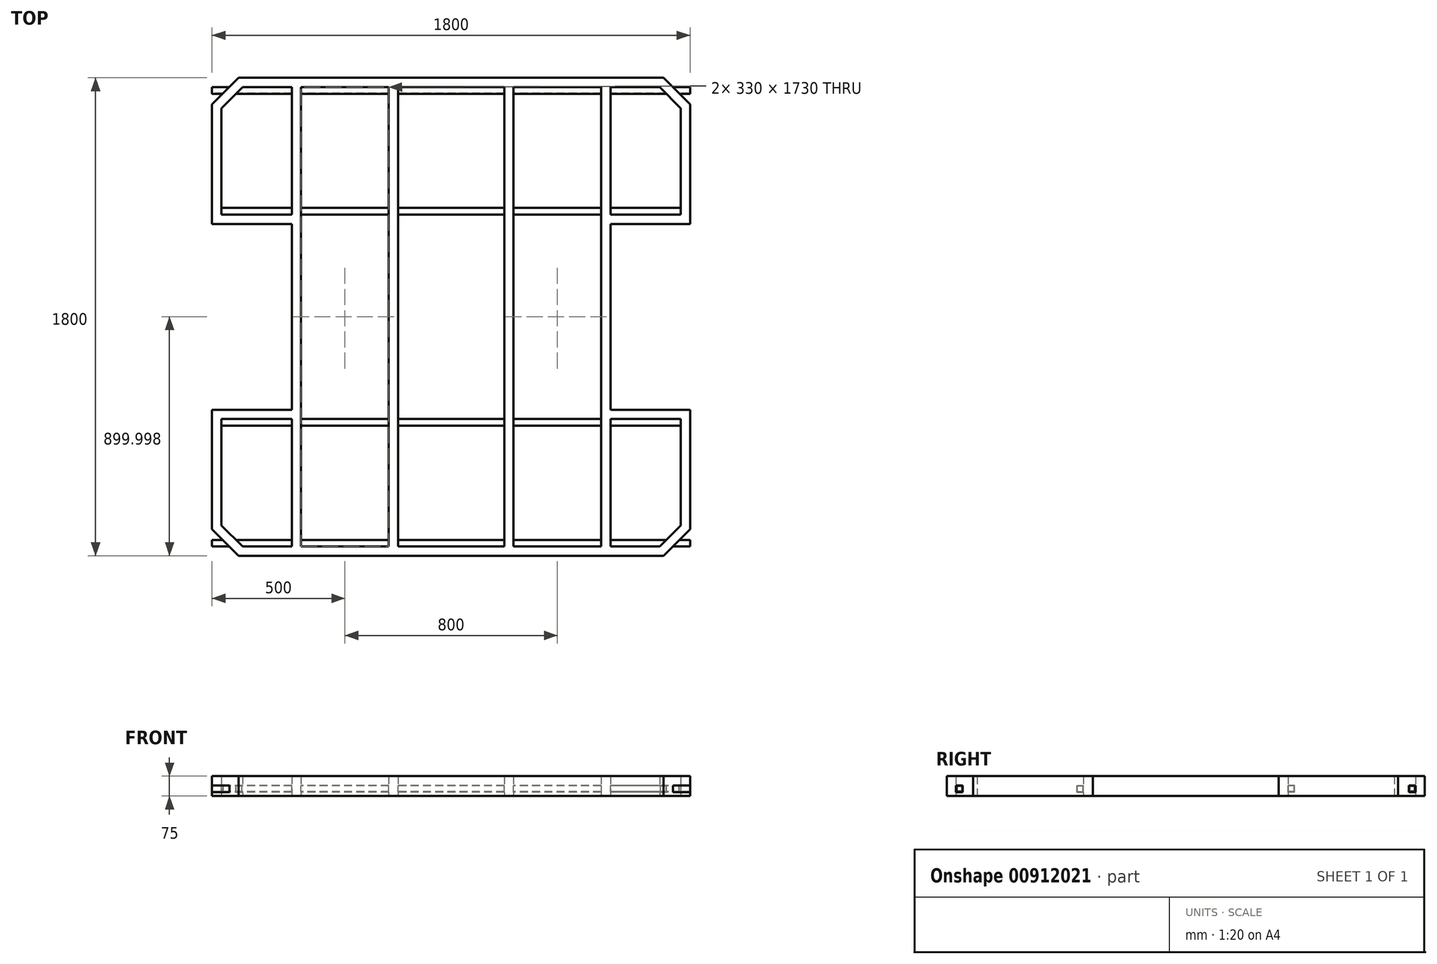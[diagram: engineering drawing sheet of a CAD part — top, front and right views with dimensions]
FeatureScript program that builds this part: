
annotation { "Feature Type Name" : "Feature", "Feature Type Description" : "" }
export const myFeature = defineFeature(function(context is Context, id is Id, definition is map)
    precondition{}
    {
        {
            var Q0;
            Q0=qCreatedBy(makeId("Top.planeOp"),FACE);
            var sketch = newSketch(context, id + "F0", { "sketchPlane" : qUnion([Q0])});
            skLineSegment(sketch, "E0.bottom", {"start": v(-100, 518.45) * mm, "end": v(-1700, 518.45) * mm});
            skLineSegment(sketch, "E0.top", {"start": v(-100, 2318.45) * mm, "end": v(-1700, 2318.45) * mm});
            skLineSegment(sketch, "E0.left", {"start": v(0, 618.45) * mm, "end": v(0, 1068.45) * mm});
            skLineSegment(sketch, "E1", {"start": v(-1800, 2218.45) * mm, "end": v(-1700, 2318.45) * mm});
            skLineSegment(sketch, "E2", {"start": v(-100, 2318.45) * mm, "end": v(0, 2218.45) * mm});
            skLineSegment(sketch, "E3", {"start": v(0, 618.45) * mm, "end": v(-100, 518.45) * mm});
            skPoint(sketch, "E4.orphan", {"position": v(-1344.08, 2218.45) * mm});
            skLineSegment(sketch, "E5", {"start": v(-1700, 518.45) * mm, "end": v(-1800, 618.45) * mm});
            skLineSegment(sketch, "E6", {"start": v(-1800, 618.45) * mm, "end": v(-1800, 1068.45) * mm});
            skLineSegment(sketch, "E7.bottom", {"start": v(-1900, 1768.45) * mm, "end": v(-1500, 1768.45) * mm});
            skLineSegment(sketch, "E7.top", {"start": v(-1900, 1068.45) * mm, "end": v(-1500, 1068.45) * mm});
            skLineSegment(sketch, "E7.left", {"start": v(-1900, 1768.45) * mm, "end": v(-1900, 1068.45) * mm});
            skLineSegment(sketch, "E7.right", {"start": v(-1500, 1768.45) * mm, "end": v(-1500, 1068.45) * mm});
            skLineSegment(sketch, "E8.bottom", {"start": v(-300, 1768.45) * mm, "end": v(100, 1768.45) * mm});
            skLineSegment(sketch, "E8.top", {"start": v(-300, 1068.45) * mm, "end": v(100, 1068.45) * mm});
            skLineSegment(sketch, "E8.left", {"start": v(-300, 1768.45) * mm, "end": v(-300, 1068.45) * mm});
            skLineSegment(sketch, "E8.right", {"start": v(100, 1768.45) * mm, "end": v(100, 1068.45) * mm});
            skLineSegment(sketch, "E9.trimOffspring", {"start": v(-1800, 1768.45) * mm, "end": v(-1800, 2218.45) * mm});
            skLineSegment(sketch, "E10.trimOffspring", {"start": v(0, 1768.45) * mm, "end": v(0, 2218.45) * mm});
            skSolve(sketch);
        }
        {
            var Q0;
            Q0=makeQuery(id+"F0.imprint","IMPRINT",FACE,{"disambiguationData":[TD([[makeQuery(id+"F0.imprint","IMPRINT",EDGE,{"derivedFrom":sQuery(id+"F0.wireOp",EDGE,"E0.bottom")}),-1.0]])]});
            var sketch = newSketch(context, id + "F1", { "sketchPlane" : qUnion([Q0])});
            skLineSegment(sketch, "E11.0.0", {"start": v(-300, 1768.45) * mm, "end": v(0, 1768.45) * mm});
            skLineSegment(sketch, "E11.0.1", {"start": v(0, 1768.45) * mm, "end": v(0, 2218.45) * mm});
            skLineSegment(sketch, "E11.0.2", {"start": v(0, 2218.45) * mm, "end": v(-100, 2318.45) * mm});
            skLineSegment(sketch, "E11.0.3", {"start": v(-100, 2318.45) * mm, "end": v(-1700, 2318.45) * mm});
            skLineSegment(sketch, "E11.0.4", {"start": v(-1700, 2318.45) * mm, "end": v(-1800, 2218.45) * mm});
            skLineSegment(sketch, "E11.0.5", {"start": v(-1800, 2218.45) * mm, "end": v(-1800, 1768.45) * mm});
            skLineSegment(sketch, "E11.0.6", {"start": v(-1800, 1768.45) * mm, "end": v(-1500, 1768.45) * mm});
            skLineSegment(sketch, "E11.0.7", {"start": v(-1500, 1768.45) * mm, "end": v(-1500, 1068.45) * mm});
            skLineSegment(sketch, "E11.0.8", {"start": v(-1500, 1068.45) * mm, "end": v(-1800, 1068.45) * mm});
            skLineSegment(sketch, "E11.0.9", {"start": v(-1800, 1068.45) * mm, "end": v(-1800, 618.45) * mm});
            skLineSegment(sketch, "E11.0.10", {"start": v(-1800, 618.45) * mm, "end": v(-1700, 518.45) * mm});
            skLineSegment(sketch, "E11.0.11", {"start": v(-1700, 518.45) * mm, "end": v(-100, 518.45) * mm});
            skLineSegment(sketch, "E11.0.12", {"start": v(-100, 518.45) * mm, "end": v(0, 618.45) * mm});
            skLineSegment(sketch, "E11.0.13", {"start": v(0, 618.45) * mm, "end": v(0, 1068.45) * mm});
            skLineSegment(sketch, "E11.0.14", {"start": v(0, 1068.45) * mm, "end": v(-300, 1068.45) * mm});
            skLineSegment(sketch, "E11.0.15", {"start": v(-300, 1068.45) * mm, "end": v(-300, 1768.45) * mm});
            skLineSegment(sketch, "E12.0", {"start": v(-335, 1033.45) * mm, "end": v(-335, 1803.45) * mm});
            skLineSegment(sketch, "E12.1", {"start": v(-35, 1033.45) * mm, "end": v(-300, 1033.45) * mm});
            skLineSegment(sketch, "E12.2", {"start": v(-35, 632.95) * mm, "end": v(-35, 1033.45) * mm});
            skLineSegment(sketch, "E12.3", {"start": v(-114.5, 553.45) * mm, "end": v(-35, 632.95) * mm});
            skLineSegment(sketch, "E12.4", {"start": v(-1685.5, 553.45) * mm, "end": v(-1500, 553.45) * mm});
            skLineSegment(sketch, "E12.5", {"start": v(-1685.5, 2283.45) * mm, "end": v(-1765, 2203.95) * mm});
            skLineSegment(sketch, "E12.6", {"start": v(-114.5, 2283.45) * mm, "end": v(-300, 2283.45) * mm});
            skLineSegment(sketch, "E12.7", {"start": v(-35, 2203.95) * mm, "end": v(-114.5, 2283.45) * mm});
            skLineSegment(sketch, "E12.8", {"start": v(-35, 1803.45) * mm, "end": v(-35, 2203.95) * mm});
            skLineSegment(sketch, "E12.9", {"start": v(-1765, 2203.95) * mm, "end": v(-1765, 1803.45) * mm});
            skLineSegment(sketch, "E12.10", {"start": v(-1765, 1803.45) * mm, "end": v(-1500, 1803.45) * mm});
            skLineSegment(sketch, "E12.11", {"start": v(-1465, 1803.45) * mm, "end": v(-1465, 1033.45) * mm});
            skLineSegment(sketch, "E12.12", {"start": v(-1500, 1033.45) * mm, "end": v(-1765, 1033.45) * mm});
            skLineSegment(sketch, "E12.13", {"start": v(-1765, 1033.45) * mm, "end": v(-1765, 632.95) * mm});
            skLineSegment(sketch, "E12.14", {"start": v(-300, 1803.45) * mm, "end": v(-35, 1803.45) * mm});
            skLineSegment(sketch, "E12.15", {"start": v(-1765, 632.95) * mm, "end": v(-1685.5, 553.45) * mm});
            skLineSegment(sketch, "E13", {"start": v(-1465, 1803.45) * mm, "end": v(-1465, 2283.45) * mm});
            skLineSegment(sketch, "E14", {"start": v(-1500, 1803.45) * mm, "end": v(-1500, 2283.45) * mm});
            skLineSegment(sketch, "E15", {"start": v(-1465, 1033.45) * mm, "end": v(-1465, 553.45) * mm});
            skLineSegment(sketch, "E16", {"start": v(-1500, 1033.45) * mm, "end": v(-1500, 553.45) * mm});
            skLineSegment(sketch, "E17", {"start": v(-335, 1033.45) * mm, "end": v(-335, 553.45) * mm});
            skLineSegment(sketch, "E18", {"start": v(-300, 1033.45) * mm, "end": v(-300, 553.45) * mm});
            skLineSegment(sketch, "E19", {"start": v(-335, 1803.45) * mm, "end": v(-335, 2283.45) * mm});
            skLineSegment(sketch, "E20", {"start": v(-300, 1803.45) * mm, "end": v(-300, 2283.45) * mm});
            skLineSegment(sketch, "E21.trimOffspring", {"start": v(-1500, 2283.45) * mm, "end": v(-1685.5, 2283.45) * mm});
            skLineSegment(sketch, "E22.trimOffspring", {"start": v(-1465, 553.45) * mm, "end": v(-1135, 553.45) * mm});
            skLineSegment(sketch, "E23.trimOffspring", {"start": v(-875, 553.45) * mm, "end": v(-700, 553.45) * mm});
            skLineSegment(sketch, "E24.trimOffspring", {"start": v(-735, 2283.45) * mm, "end": v(-1100, 2283.45) * mm});
            skLineSegment(sketch, "E25", {"start": v(-875, 2283.45) * mm, "end": v(-735, 2283.45) * mm});
            skLineSegment(sketch, "E26", {"start": v(-875, 553.45) * mm, "end": v(-735, 553.45) * mm});
            skLineSegment(sketch, "E27", {"start": v(-1135, 2283.45) * mm, "end": v(-1135, 553.45) * mm});
            skLineSegment(sketch, "E28", {"start": v(-1100, 2283.45) * mm, "end": v(-1100, 553.45) * mm});
            skLineSegment(sketch, "E29", {"start": v(-700, 2283.45) * mm, "end": v(-700, 553.45) * mm});
            skLineSegment(sketch, "E30", {"start": v(-665, 2283.45) * mm, "end": v(-665, 553.45) * mm});
            skLineSegment(sketch, "E31.trimOffspring", {"start": v(-1135, 2283.45) * mm, "end": v(-1465, 2283.45) * mm});
            skLineSegment(sketch, "E32.trimOffspring", {"start": v(-700, 2283.45) * mm, "end": v(-875, 2283.45) * mm});
            skLineSegment(sketch, "E33.trimOffspring", {"start": v(-335, 2283.45) * mm, "end": v(-665, 2283.45) * mm});
            skLineSegment(sketch, "E34.trimOffspring", {"start": v(-300, 553.45) * mm, "end": v(-114.5, 553.45) * mm});
            skLineSegment(sketch, "E35.trimOffspring", {"start": v(-665, 553.45) * mm, "end": v(-335, 553.45) * mm});
            skLineSegment(sketch, "E36.trimOffspring", {"start": v(-1100, 553.45) * mm, "end": v(-735, 553.45) * mm});
            skSolve(sketch);
        }
        {
            var Q0;
            Q0 = qSketchRegion(id + "F1", true);
            extrude(context, id + "F2", {"entities" : qUnion([Q0]), "depth" : 75 * mm, "offsetDistance" : 25 * mm});
        }
        {
            var Q0;
            Q0=makeQuery(id+"F2.opExtrude","SWEPT_FACE",FACE,{"disambiguationData":[OSD([sQuery(id+"F1.wireOp",EDGE,"E11.0.9")])]});
            var sketch = newSketch(context, id + "F3", { "sketchPlane" : qUnion([Q0])});
            skLineSegment(sketch, "E37.0.1", {"start": v(-553.45, 15) * mm, "end": v(-553.45, 75) * mm});
            skLineSegment(sketch, "E37.0.2", {"start": v(-553.45, 75) * mm, "end": v(-1033.45, 75) * mm});
            skLineSegment(sketch, "E37.0.3", {"start": v(-1033.45, 75) * mm, "end": v(-1033.45, 15) * mm});
            skLineSegment(sketch, "E38.bottom", {"start": v(-1033.45, 40) * mm, "end": v(-1008.45, 40) * mm});
            skLineSegment(sketch, "E38.top", {"start": v(-1033.45, 15) * mm, "end": v(-1008.45, 15) * mm});
            skLineSegment(sketch, "E38.left", {"start": v(-1033.45, 40) * mm, "end": v(-1033.45, 15) * mm});
            skLineSegment(sketch, "E38.right", {"start": v(-1008.45, 40) * mm, "end": v(-1008.45, 15) * mm});
            skLineSegment(sketch, "E39.bottom", {"start": v(-553.45, 40) * mm, "end": v(-578.45, 40) * mm});
            skLineSegment(sketch, "E39.top", {"start": v(-553.45, 15) * mm, "end": v(-578.45, 15) * mm});
            skLineSegment(sketch, "E39.left", {"start": v(-553.45, 40) * mm, "end": v(-553.45, 15) * mm});
            skLineSegment(sketch, "E39.right", {"start": v(-578.45, 40) * mm, "end": v(-578.45, 15) * mm});
            skPoint(sketch, "E40.orphan", {"position": v(-1033.45, 0) * mm});
            skPoint(sketch, "E41.orphan", {"position": v(-553.45, 0) * mm});
            skLineSegment(sketch, "E42.0", {"start": v(-1031.85, 38.4) * mm, "end": v(-1010.05, 38.4) * mm});
            skLineSegment(sketch, "E42.1", {"start": v(-1031.85, 38.4) * mm, "end": v(-1031.85, 16.6) * mm});
            skLineSegment(sketch, "E42.2", {"start": v(-1031.85, 16.6) * mm, "end": v(-1010.05, 16.6) * mm});
            skLineSegment(sketch, "E42.3", {"start": v(-1010.05, 38.4) * mm, "end": v(-1010.05, 16.6) * mm});
            skLineSegment(sketch, "E43.0", {"start": v(-555.05, 38.4) * mm, "end": v(-576.85, 38.4) * mm});
            skLineSegment(sketch, "E43.1", {"start": v(-555.05, 38.4) * mm, "end": v(-555.05, 16.6) * mm});
            skLineSegment(sketch, "E43.2", {"start": v(-555.05, 16.6) * mm, "end": v(-576.85, 16.6) * mm});
            skLineSegment(sketch, "E43.3", {"start": v(-576.85, 38.4) * mm, "end": v(-576.85, 16.6) * mm});
            skSolve(sketch);
        }
        {
            var Q0;
            Q0 = qSketchRegion(id + "F3", true);
            extrude(context, id + "F4", {"entities" : qUnion([Q0]), "operationType" : NewBodyOperationType.ADD, "oppositeDirection" : true, "depth" : 1800 * mm, "offsetDistance" : 25 * mm});
        }
        {
            var Q0;
            Q0=makeQuery(id+"F2.opExtrude","CAP_FACE",FACE,{"disambiguationData":[OSD([sQuery(id+"F1.wireOp",EDGE,"E11.0.0"),sQuery(id+"F1.wireOp",EDGE,"E11.0.1"),sQuery(id+"F1.wireOp",EDGE,"E11.0.2"),sQuery(id+"F1.wireOp",EDGE,"E11.0.3"),sQuery(id+"F1.wireOp",EDGE,"E11.0.4"),sQuery(id+"F1.wireOp",EDGE,"E11.0.5"),sQuery(id+"F1.wireOp",EDGE,"E11.0.6"),sQuery(id+"F1.wireOp",EDGE,"E11.0.7"),sQuery(id+"F1.wireOp",EDGE,"E11.0.8"),sQuery(id+"F1.wireOp",EDGE,"E11.0.9"),sQuery(id+"F1.wireOp",EDGE,"E11.0.10"),sQuery(id+"F1.wireOp",EDGE,"E11.0.11"),sQuery(id+"F1.wireOp",EDGE,"E11.0.12"),sQuery(id+"F1.wireOp",EDGE,"E11.0.13"),sQuery(id+"F1.wireOp",EDGE,"E11.0.14"),sQuery(id+"F1.wireOp",EDGE,"E11.0.15"),sQuery(id+"F1.wireOp",EDGE,"E12.0"),sQuery(id+"F1.wireOp",EDGE,"E12.1"),sQuery(id+"F1.wireOp",EDGE,"E12.2"),sQuery(id+"F1.wireOp",EDGE,"E12.3"),sQuery(id+"F1.wireOp",EDGE,"E12.4"),sQuery(id+"F1.wireOp",EDGE,"E12.5"),sQuery(id+"F1.wireOp",EDGE,"E12.6"),sQuery(id+"F1.wireOp",EDGE,"E12.7"),sQuery(id+"F1.wireOp",EDGE,"E12.8"),sQuery(id+"F1.wireOp",EDGE,"E12.9"),sQuery(id+"F1.wireOp",EDGE,"E12.10"),sQuery(id+"F1.wireOp",EDGE,"E12.11"),sQuery(id+"F1.wireOp",EDGE,"E12.12"),sQuery(id+"F1.wireOp",EDGE,"E12.13"),sQuery(id+"F1.wireOp",EDGE,"E12.14"),sQuery(id+"F1.wireOp",EDGE,"E12.15"),sQuery(id+"F1.wireOp",EDGE,"E13"),sQuery(id+"F1.wireOp",EDGE,"E14"),sQuery(id+"F1.wireOp",EDGE,"E15"),sQuery(id+"F1.wireOp",EDGE,"E16"),sQuery(id+"F1.wireOp",EDGE,"E17"),sQuery(id+"F1.wireOp",EDGE,"E18"),sQuery(id+"F1.wireOp",EDGE,"E19"),sQuery(id+"F1.wireOp",EDGE,"E20"),sQuery(id+"F1.wireOp",EDGE,"E21.trimOffspring"),sQuery(id+"F1.wireOp",EDGE,"E22.trimOffspring"),sQuery(id+"F1.wireOp",EDGE,"E23.trimOffspring"),sQuery(id+"F1.wireOp",EDGE,"E24.trimOffspring"),sQuery(id+"F1.wireOp",EDGE,"E27"),sQuery(id+"F1.wireOp",EDGE,"E28"),sQuery(id+"F1.wireOp",EDGE,"E29"),sQuery(id+"F1.wireOp",EDGE,"E30"),sQuery(id+"F1.wireOp",EDGE,"E31.trimOffspring"),sQuery(id+"F1.wireOp",EDGE,"E32.trimOffspring"),sQuery(id+"F1.wireOp",EDGE,"E33.trimOffspring"),sQuery(id+"F1.wireOp",EDGE,"E34.trimOffspring"),sQuery(id+"F1.wireOp",EDGE,"E35.trimOffspring"),sQuery(id+"F1.wireOp",EDGE,"E36.trimOffspring")])],"isStart":false});
            var sketch = newSketch(context, id + "F5", { "sketchPlane" : qUnion([Q0])});
            skLineSegment(sketch, "E44", {"start": v(-1500, 1418.45) * mm, "end": v(-300, 1418.45) * mm});
            skSolve(sketch);
        }
        {
            var Q0;
            Q0=makeQuery(id+"F2.opExtrude","SWEPT_FACE",FACE,{"disambiguationData":[OSD([sQuery(id+"F1.wireOp",EDGE,"E11.0.3")])]});
            cPlane(context, id + "F6", {"entities" : qUnion([Q0]), "cplaneType" : CPlaneType.OFFSET, "offset" : 900 * mm, "oppositeDirection" : true, "width" : 150 * mm, "height" : 150 * mm});
        }
        {
            var Q0;
            Q0=makeQuery(id+"F2.opExtrude","SWEPT_BODY",BODY,{"disambiguationData":[OSD([sQuery(id+"F1.wireOp",EDGE,"E11.0.0"),sQuery(id+"F1.wireOp",EDGE,"E11.0.1"),sQuery(id+"F1.wireOp",EDGE,"E11.0.2"),sQuery(id+"F1.wireOp",EDGE,"E11.0.3"),sQuery(id+"F1.wireOp",EDGE,"E11.0.4"),sQuery(id+"F1.wireOp",EDGE,"E11.0.5"),sQuery(id+"F1.wireOp",EDGE,"E11.0.6"),sQuery(id+"F1.wireOp",EDGE,"E11.0.7"),sQuery(id+"F1.wireOp",EDGE,"E11.0.8"),sQuery(id+"F1.wireOp",EDGE,"E11.0.9"),sQuery(id+"F1.wireOp",EDGE,"E11.0.10"),sQuery(id+"F1.wireOp",EDGE,"E11.0.11"),sQuery(id+"F1.wireOp",EDGE,"E11.0.12"),sQuery(id+"F1.wireOp",EDGE,"E11.0.13"),sQuery(id+"F1.wireOp",EDGE,"E11.0.14"),sQuery(id+"F1.wireOp",EDGE,"E11.0.15"),sQuery(id+"F1.wireOp",EDGE,"E12.0"),sQuery(id+"F1.wireOp",EDGE,"E12.1"),sQuery(id+"F1.wireOp",EDGE,"E12.2"),sQuery(id+"F1.wireOp",EDGE,"E12.3"),sQuery(id+"F1.wireOp",EDGE,"E12.4"),sQuery(id+"F1.wireOp",EDGE,"E12.5"),sQuery(id+"F1.wireOp",EDGE,"E12.6"),sQuery(id+"F1.wireOp",EDGE,"E12.7"),sQuery(id+"F1.wireOp",EDGE,"E12.8"),sQuery(id+"F1.wireOp",EDGE,"E12.9"),sQuery(id+"F1.wireOp",EDGE,"E12.10"),sQuery(id+"F1.wireOp",EDGE,"E12.11"),sQuery(id+"F1.wireOp",EDGE,"E12.12"),sQuery(id+"F1.wireOp",EDGE,"E12.13"),sQuery(id+"F1.wireOp",EDGE,"E12.14"),sQuery(id+"F1.wireOp",EDGE,"E12.15"),sQuery(id+"F1.wireOp",EDGE,"E13"),sQuery(id+"F1.wireOp",EDGE,"E14"),sQuery(id+"F1.wireOp",EDGE,"E15"),sQuery(id+"F1.wireOp",EDGE,"E16"),sQuery(id+"F1.wireOp",EDGE,"E17"),sQuery(id+"F1.wireOp",EDGE,"E18"),sQuery(id+"F1.wireOp",EDGE,"E19"),sQuery(id+"F1.wireOp",EDGE,"E20"),sQuery(id+"F1.wireOp",EDGE,"E21.trimOffspring"),sQuery(id+"F1.wireOp",EDGE,"E22.trimOffspring"),sQuery(id+"F1.wireOp",EDGE,"E23.trimOffspring"),sQuery(id+"F1.wireOp",EDGE,"E24.trimOffspring"),sQuery(id+"F1.wireOp",EDGE,"E27"),sQuery(id+"F1.wireOp",EDGE,"E28"),sQuery(id+"F1.wireOp",EDGE,"E29"),sQuery(id+"F1.wireOp",EDGE,"E30"),sQuery(id+"F1.wireOp",EDGE,"E31.trimOffspring"),sQuery(id+"F1.wireOp",EDGE,"E32.trimOffspring"),sQuery(id+"F1.wireOp",EDGE,"E33.trimOffspring"),sQuery(id+"F1.wireOp",EDGE,"E34.trimOffspring"),sQuery(id+"F1.wireOp",EDGE,"E35.trimOffspring"),sQuery(id+"F1.wireOp",EDGE,"E36.trimOffspring")])]});
            var Q1;
            Q1=qCreatedBy(id+"F6.planeOp",FACE);
            mirror(context, id + "F7", {"operationType" : NewBodyOperationType.ADD, "entities" : qUnion([Q0]), "mirrorPlane" : qUnion([Q1])});
        }
        {
            var Q0;
            Q0=makeQuery(id+"F2.opExtrude","SWEPT_FACE",FACE,{"disambiguationData":[OSD([sQuery(id+"F1.wireOp",EDGE,"E11.0.15")])]});
            var sketch = newSketch(context, id + "F8", { "sketchPlane" : qUnion([Q0])});
            skLineSegment(sketch, "E45.bottom", {"start": v(1405.95, 40) * mm, "end": v(1430.95, 40) * mm});
            skLineSegment(sketch, "E45.top", {"start": v(1405.95, 15) * mm, "end": v(1430.95, 15) * mm});
            skLineSegment(sketch, "E45.left", {"start": v(1405.95, 40) * mm, "end": v(1405.95, 15) * mm});
            skLineSegment(sketch, "E45.right", {"start": v(1430.95, 40) * mm, "end": v(1430.95, 15) * mm});
            skLineSegment(sketch, "E46.0", {"start": v(1407.55, 38.4) * mm, "end": v(1429.35, 38.4) * mm});
            skLineSegment(sketch, "E46.1", {"start": v(1407.55, 38.4) * mm, "end": v(1407.55, 16.6) * mm});
            skLineSegment(sketch, "E46.2", {"start": v(1407.55, 16.6) * mm, "end": v(1429.35, 16.6) * mm});
            skLineSegment(sketch, "E46.3", {"start": v(1429.35, 38.4) * mm, "end": v(1429.35, 16.6) * mm});
            skLineSegment(sketch, "E47.0", {"start": v(1073.45, 5) * mm, "end": v(1763.45, 5) * mm});
            skLineSegment(sketch, "E47.1", {"start": v(1073.45, 70) * mm, "end": v(1073.45, 5) * mm});
            skLineSegment(sketch, "E47.2", {"start": v(1763.45, 70) * mm, "end": v(1073.45, 70) * mm});
            skLineSegment(sketch, "E47.3", {"start": v(1763.45, 5) * mm, "end": v(1763.45, 70) * mm});
            skSolve(sketch);
        }
        {
            var Q0;
            Q0=sQuery(id+"F8.wireOp",EDGE,"E46.0");
            var Q1;
            Q1=sQuery(id+"F8.wireOp",EDGE,"E45.bottom");
            var Q2;
            Q2=sQuery(id+"F8.wireOp",EDGE,"E45.left");
            var Q3;
            Q3=sQuery(id+"F8.wireOp",EDGE,"E46.1");
            var Q4;
            Q4=sQuery(id+"F8.wireOp",EDGE,"E46.3");
            var Q5;
            Q5=sQuery(id+"F8.wireOp",EDGE,"E45.right");
            var Q6;
            Q6=sQuery(id+"F8.wireOp",EDGE,"E46.2");
            var Q7;
            Q7=sQuery(id+"F8.wireOp",EDGE,"E45.top");
            extrude(context, id + "F9", {"bodyType" : ToolBodyType.SURFACE, "surfaceEntities" : qUnion([Q0, Q1, Q2, Q3, Q4, Q5, Q6, Q7]), "oppositeDirection" : true, "depth" : 1200 * mm, "offsetDistance" : 25 * mm});
        }
    });
